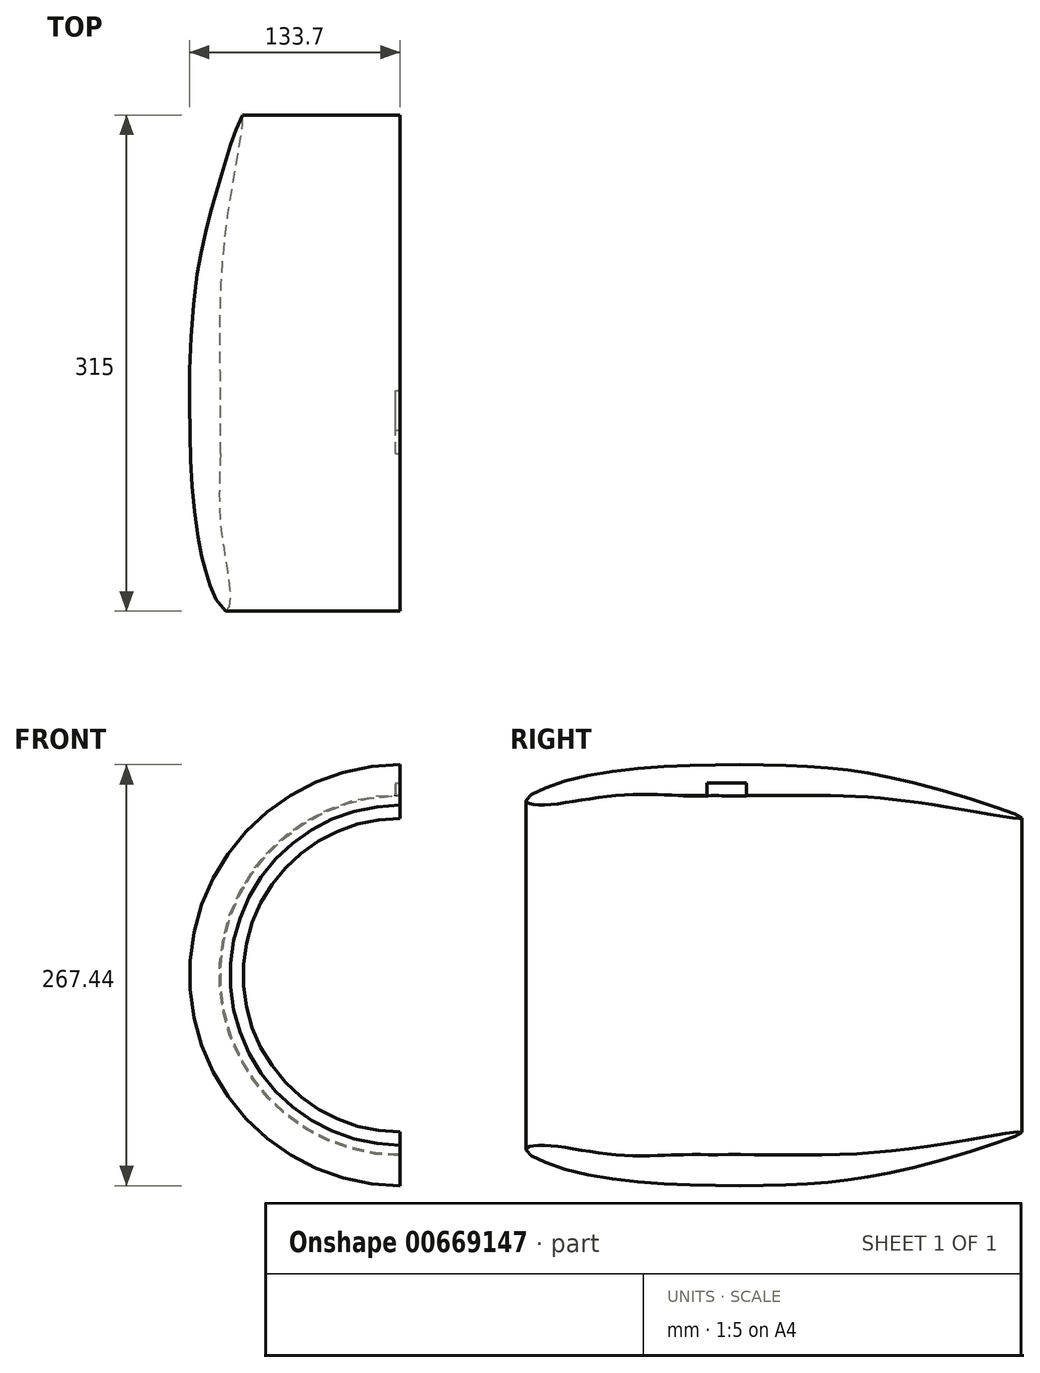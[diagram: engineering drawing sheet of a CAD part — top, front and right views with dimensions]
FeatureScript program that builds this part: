
annotation { "Feature Type Name" : "Feature", "Feature Type Description" : "" }
export const myFeature = defineFeature(function(context is Context, id is Id, definition is map)
    precondition{}
    {
        {
            var Q0;
            Q0=qCreatedBy(makeId("Right.planeOp"),FACE);
            var sketch = newSketch(context, id + "F0", { "sketchPlane" : qUnion([Q0])});
            skLineSegment(sketch, "E0", {"start": v(0, 0) * mm, "end": v(43.54, 0) * mm, "construction": true});
            skFitSpline(sketch, "E1", {"points": [v(-15, 114) * mm, v(-59.32, 114) * mm, v(-106.5, 108) * mm, v(-115, 111) * mm, v(-86.43, 124.38) * mm, v(0, 133.53) * mm, v(70.83, 131.97) * mm, v(135.31, 121.04) * mm, v(200, 100) * mm, v(152.8, 106.83) * mm, v(84.5, 113.94) * mm, v(25, 114) * mm, v(0, 114) * mm, v(-15, 114) * mm]});
            skSolve(sketch);
        }
        {
            var Q0;
            Q0 = qSketchRegion(id + "F0", true);
            var Q1;
            Q1=sQuery(id+"F0.wireOp",EDGE,"E0");
            revolve(context, id + "F1", {"entities" : qUnion([Q0]), "axis" : qUnion([Q1]), "revolveType" : RevolveType.ONE_DIRECTION, "oppositeDirection" : true, "angle" : 180 * degree});
        }
        {
            var Q0;
            Q0=qCreatedBy(makeId("Right.planeOp"),FACE);
            var sketch = newSketch(context, id + "F2", { "sketchPlane" : qUnion([Q0])});
            skLineSegment(sketch, "E2", {"start": v(-15, 114) * mm, "end": v(0, 114) * mm});
            skLineSegment(sketch, "E3", {"start": v(0, 114) * mm, "end": v(0, 122.04) * mm});
            skLineSegment(sketch, "E4", {"start": v(0, 122.04) * mm, "end": v(25, 122.04) * mm});
            skLineSegment(sketch, "E5", {"start": v(25, 122.04) * mm, "end": v(25, 112) * mm});
            skLineSegment(sketch, "E6", {"start": v(25, 112) * mm, "end": v(-15, 112) * mm});
            skLineSegment(sketch, "E7", {"start": v(-15, 112) * mm, "end": v(-15, 114) * mm});
            skSolve(sketch);
        }
        {
            var Q0;
            Q0 = qSketchRegion(id + "F2", true);
            extrude(context, id + "F3", {"entities" : qUnion([Q0]), "operationType" : NewBodyOperationType.REMOVE, "oppositeDirection" : true, "depth" : 3 * mm, "offsetDistance" : 25 * mm});
        }
    });
